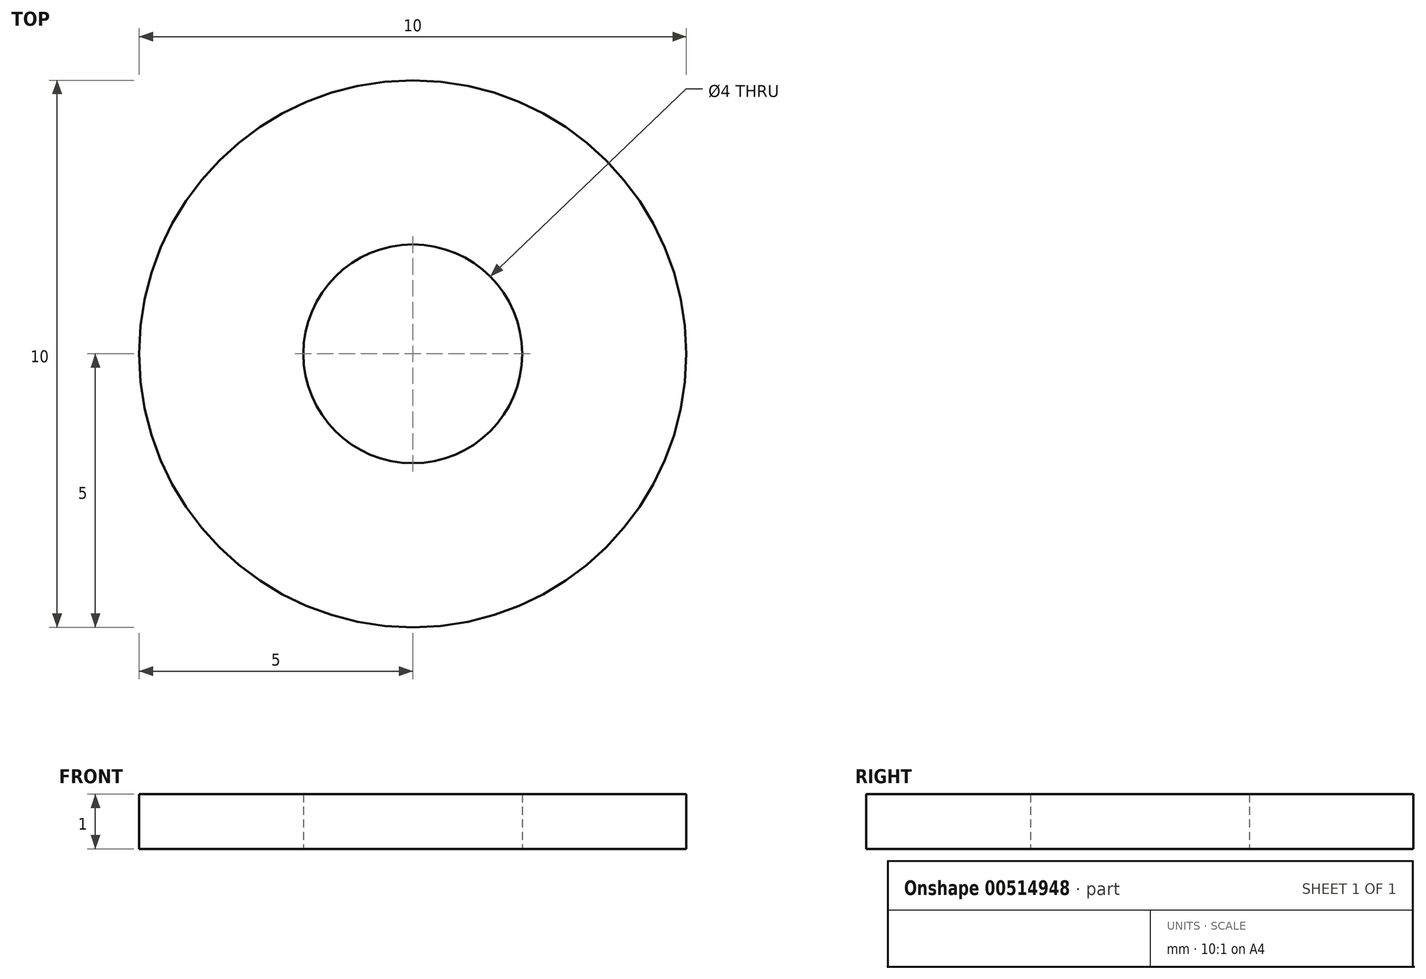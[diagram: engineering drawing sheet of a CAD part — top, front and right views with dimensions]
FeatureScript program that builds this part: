
annotation { "Feature Type Name" : "Feature", "Feature Type Description" : "" }
export const myFeature = defineFeature(function(context is Context, id is Id, definition is map)
    precondition{}
    {
        {
            var Q0;
            Q0=qCreatedBy(makeId("Top.planeOp"),FACE);
            var sketch = newSketch(context, id + "F0", { "sketchPlane" : qUnion([Q0])});
            skCircle(sketch, "E0", {"center": v(0, 0) * mm, "radius": 2 * mm});
            skCircle(sketch, "E1", {"center": v(0, 0) * mm, "radius": 5 * mm});
            skSolve(sketch);
        }
        {
            var Q0;
            Q0=makeQuery(id+"F0.imprint","IMPRINT",FACE,{"disambiguationData":[TD([[makeQuery(id+"F0.imprint","IMPRINT",EDGE,{"derivedFrom":sQuery(id+"F0.wireOp",EDGE,"E0")}),-1.0]])]});
            extrude(context, id + "F1", {"entities" : qUnion([Q0]), "depth" : 1 * mm, "offsetDistance" : 25 * mm});
        }
    });
